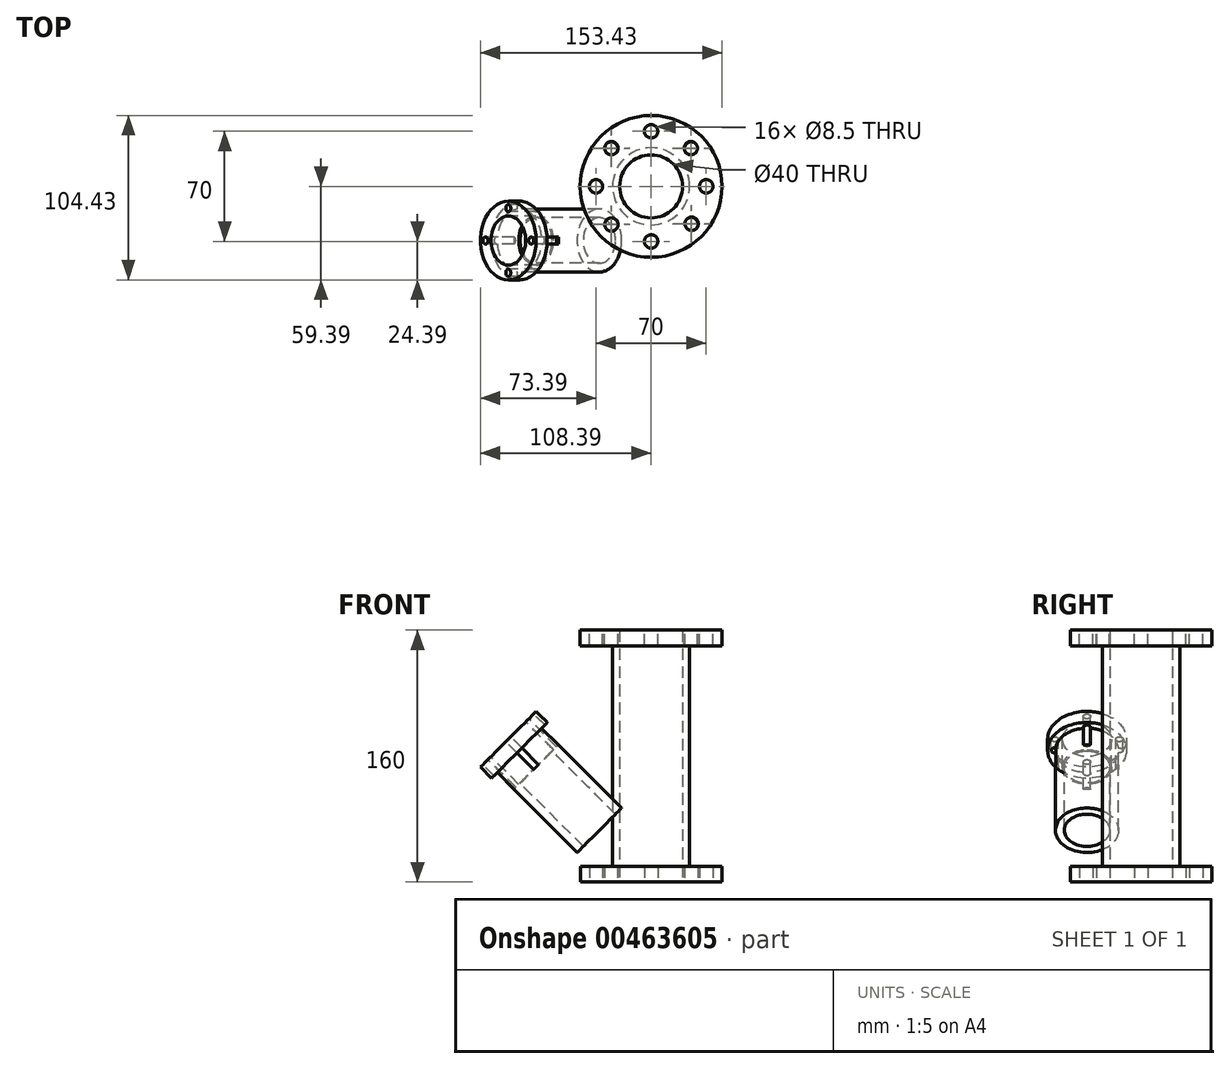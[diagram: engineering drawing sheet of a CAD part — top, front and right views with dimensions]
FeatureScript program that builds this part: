
annotation { "Feature Type Name" : "Feature", "Feature Type Description" : "" }
export const myFeature = defineFeature(function(context is Context, id is Id, definition is map)
    precondition{}
    {
        {
            var Q0;
            Q0=qCreatedBy(makeId("Top.planeOp"),FACE);
            var sketch = newSketch(context, id + "F0", { "sketchPlane" : qUnion([Q0])});
            skCircle(sketch, "E0", {"center": v(0, 0) * mm, "radius": 45 * mm});
            skSolve(sketch);
        }
        {
            var Q0;
            Q0=makeQuery(id+"F0.imprint","IMPRINT",FACE,{"disambiguationData":[TD([[makeQuery(id+"F0.imprint","IMPRINT",EDGE,{"derivedFrom":sQuery(id+"F0.wireOp",EDGE,"E0")}),1.0]])]});
            extrude(context, id + "F1", {"entities" : qUnion([Q0]), "depth" : 10 * mm});
        }
        {
            var Q0;
            Q0=makeQuery(id+"F1.opExtrude","CAP_FACE",FACE,{"disambiguationData":[OSD([sQuery(id+"F0.wireOp",EDGE,"E0")])],"isStart":false});
            var sketch = newSketch(context, id + "F2", { "sketchPlane" : qUnion([Q0])});
            skCircle(sketch, "E1", {"center": v(0, 0) * mm, "radius": 24.5 * mm});
            skSolve(sketch);
        }
        {
            var Q0;
            Q0=makeQuery(id+"F2.imprint","IMPRINT",FACE,{"disambiguationData":[TD([[makeQuery(id+"F2.imprint","IMPRINT",EDGE,{"derivedFrom":sQuery(id+"F2.wireOp",EDGE,"E1")}),1.0]])]});
            extrude(context, id + "F3", {"entities" : qUnion([Q0]), "operationType" : NewBodyOperationType.ADD, "depth" : 140 * mm});
        }
        {
            var Q0;
            Q0=makeQuery(id+"F3.opExtrude","CAP_FACE",FACE,{"disambiguationData":[OSD([sQuery(id+"F2.wireOp",EDGE,"E1")])],"isStart":false});
            var sketch = newSketch(context, id + "F4", { "sketchPlane" : qUnion([Q0])});
            skCircle(sketch, "E2", {"center": v(0, 0) * mm, "radius": 45.04 * mm});
            skSolve(sketch);
        }
        {
            var Q0;
            Q0 = qSketchRegion(id + "F4", true);
            extrude(context, id + "F5", {"entities" : qUnion([Q0]), "operationType" : NewBodyOperationType.ADD, "depth" : 10 * mm});
        }
        {
            var Q0;
            Q0=makeQuery(id+"F1.opExtrude","CAP_FACE",FACE,{"disambiguationData":[OSD([sQuery(id+"F0.wireOp",EDGE,"E0")])],"isStart":true});
            var sketch = newSketch(context, id + "F6", { "sketchPlane" : qUnion([Q0])});
            skCircle(sketch, "E3", {"center": v(0, 0) * mm, "radius": 20 * mm});
            skSolve(sketch);
        }
        {
            var Q0;
            Q0=makeQuery(id+"F6.imprint","IMPRINT",FACE,{"disambiguationData":[TD([[makeQuery(id+"F6.imprint","IMPRINT",EDGE,{"derivedFrom":sQuery(id+"F6.wireOp",EDGE,"E3")}),1.0]])]});
            extrude(context, id + "F7", {"entities" : qUnion([Q0]), "operationType" : NewBodyOperationType.REMOVE, "oppositeDirection" : true, "depth" : 160 * mm});
        }
        {
            var Q0;
            Q0=makeQuery(id+"F5.opExtrude","CAP_FACE",FACE,{"disambiguationData":[OSD([sQuery(id+"F4.wireOp",EDGE,"E2")])],"isStart":false});
            var sketch = newSketch(context, id + "F8", { "sketchPlane" : qUnion([Q0])});
            skCircle(sketch, "E4", {"center": v(0, 35) * mm, "radius": 4.25 * mm});
            skCircle(sketch, "E5", {"center": v(35, 0) * mm, "radius": 4.25 * mm});
            skCircle(sketch, "E6", {"center": v(0, -35) * mm, "radius": 4.25 * mm});
            skCircle(sketch, "E7", {"center": v(-35, 0) * mm, "radius": 4.25 * mm});
            skCircle(sketch, "E8", {"center": v(-25.23, 24.26) * mm, "radius": 4.25 * mm});
            skCircle(sketch, "E9", {"center": v(25.73, -23.73) * mm, "radius": 4.25 * mm});
            skCircle(sketch, "E10", {"center": v(25.23, 24.26) * mm, "radius": 4.25 * mm});
            skCircle(sketch, "E11", {"center": v(-25.23, -24.26) * mm, "radius": 4.25 * mm});
            skSolve(sketch);
        }
        {
            var Q0;
            Q0=makeQuery(id+"F8.imprint","IMPRINT",FACE,{"disambiguationData":[TD([[makeQuery(id+"F8.imprint","IMPRINT",EDGE,{"derivedFrom":sQuery(id+"F8.wireOp",EDGE,"E8")}),1.0]])]});
            var Q1;
            Q1=makeQuery(id+"F8.imprint","IMPRINT",FACE,{"disambiguationData":[TD([[makeQuery(id+"F8.imprint","IMPRINT",EDGE,{"derivedFrom":sQuery(id+"F8.wireOp",EDGE,"E10")}),1.0]])]});
            var Q2;
            Q2=makeQuery(id+"F8.imprint","IMPRINT",FACE,{"disambiguationData":[TD([[makeQuery(id+"F8.imprint","IMPRINT",EDGE,{"derivedFrom":sQuery(id+"F8.wireOp",EDGE,"E4")}),1.0]])]});
            var Q3;
            Q3=makeQuery(id+"F8.imprint","IMPRINT",FACE,{"disambiguationData":[TD([[makeQuery(id+"F8.imprint","IMPRINT",EDGE,{"derivedFrom":sQuery(id+"F8.wireOp",EDGE,"E5")}),1.0]])]});
            var Q4;
            Q4=makeQuery(id+"F8.imprint","IMPRINT",FACE,{"disambiguationData":[TD([[makeQuery(id+"F8.imprint","IMPRINT",EDGE,{"derivedFrom":sQuery(id+"F8.wireOp",EDGE,"E9")}),1.0]])]});
            var Q5;
            Q5=makeQuery(id+"F8.imprint","IMPRINT",FACE,{"disambiguationData":[TD([[makeQuery(id+"F8.imprint","IMPRINT",EDGE,{"derivedFrom":sQuery(id+"F8.wireOp",EDGE,"E6")}),1.0]])]});
            var Q6;
            Q6=makeQuery(id+"F8.imprint","IMPRINT",FACE,{"disambiguationData":[TD([[makeQuery(id+"F8.imprint","IMPRINT",EDGE,{"derivedFrom":sQuery(id+"F8.wireOp",EDGE,"E11")}),1.0]])]});
            var Q7;
            Q7=makeQuery(id+"F8.imprint","IMPRINT",FACE,{"disambiguationData":[TD([[makeQuery(id+"F8.imprint","IMPRINT",EDGE,{"derivedFrom":sQuery(id+"F8.wireOp",EDGE,"E7")}),1.0]])]});
            extrude(context, id + "F9", {"entities" : qUnion([Q0, Q1, Q2, Q3, Q4, Q5, Q6, Q7]), "operationType" : NewBodyOperationType.REMOVE, "oppositeDirection" : true, "depth" : 25 * mm});
        }
        {
            var Q0;
            Q0=makeQuery(id+"F1.opExtrude","CAP_FACE",FACE,{"disambiguationData":[OSD([sQuery(id+"F0.wireOp",EDGE,"E0")])],"isStart":true});
            var sketch = newSketch(context, id + "F10", { "sketchPlane" : qUnion([Q0])});
            skCircle(sketch, "E12", {"center": v(0, 35) * mm, "radius": 4.25 * mm});
            skCircle(sketch, "E13", {"center": v(35, 0) * mm, "radius": 4.25 * mm});
            skCircle(sketch, "E14", {"center": v(0, -35) * mm, "radius": 4.25 * mm});
            skCircle(sketch, "E15", {"center": v(-35, 0) * mm, "radius": 4.25 * mm});
            skCircle(sketch, "E16", {"center": v(-25.46, 24.01) * mm, "radius": 4.25 * mm});
            skCircle(sketch, "E17", {"center": v(25.46, 24.01) * mm, "radius": 4.25 * mm});
            skCircle(sketch, "E18", {"center": v(25.46, -24.01) * mm, "radius": 4.25 * mm});
            skCircle(sketch, "E19", {"center": v(-25.46, -24.01) * mm, "radius": 4.25 * mm});
            skPoint(sketch, "E20.center.orphan", {"position": v(0, 0) * mm});
            skSolve(sketch);
        }
        {
            var Q0;
            Q0=makeQuery(id+"F10.imprint","IMPRINT",FACE,{"disambiguationData":[TD([[makeQuery(id+"F10.imprint","IMPRINT",EDGE,{"derivedFrom":sQuery(id+"F10.wireOp",EDGE,"E16")}),1.0]])]});
            var Q1;
            Q1=makeQuery(id+"F10.imprint","IMPRINT",FACE,{"disambiguationData":[TD([[makeQuery(id+"F10.imprint","IMPRINT",EDGE,{"derivedFrom":sQuery(id+"F10.wireOp",EDGE,"E12")}),1.0]])]});
            var Q2;
            Q2=makeQuery(id+"F10.imprint","IMPRINT",FACE,{"disambiguationData":[TD([[makeQuery(id+"F10.imprint","IMPRINT",EDGE,{"derivedFrom":sQuery(id+"F10.wireOp",EDGE,"E17")}),1.0]])]});
            var Q3;
            Q3=makeQuery(id+"F10.imprint","IMPRINT",FACE,{"disambiguationData":[TD([[makeQuery(id+"F10.imprint","IMPRINT",EDGE,{"derivedFrom":sQuery(id+"F10.wireOp",EDGE,"E13")}),1.0]])]});
            var Q4;
            Q4=makeQuery(id+"F10.imprint","IMPRINT",FACE,{"disambiguationData":[TD([[makeQuery(id+"F10.imprint","IMPRINT",EDGE,{"derivedFrom":sQuery(id+"F10.wireOp",EDGE,"E18")}),1.0]])]});
            var Q5;
            Q5=makeQuery(id+"F10.imprint","IMPRINT",FACE,{"disambiguationData":[TD([[makeQuery(id+"F10.imprint","IMPRINT",EDGE,{"derivedFrom":sQuery(id+"F10.wireOp",EDGE,"E14")}),1.0]])]});
            var Q6;
            Q6=makeQuery(id+"F10.imprint","IMPRINT",FACE,{"disambiguationData":[TD([[makeQuery(id+"F10.imprint","IMPRINT",EDGE,{"derivedFrom":sQuery(id+"F10.wireOp",EDGE,"E19")}),1.0]])]});
            var Q7;
            Q7=makeQuery(id+"F10.imprint","IMPRINT",FACE,{"disambiguationData":[TD([[makeQuery(id+"F10.imprint","IMPRINT",EDGE,{"derivedFrom":sQuery(id+"F10.wireOp",EDGE,"E15")}),1.0]])]});
            extrude(context, id + "F11", {"entities" : qUnion([Q0, Q1, Q2, Q3, Q4, Q5, Q6, Q7]), "operationType" : NewBodyOperationType.REMOVE, "oppositeDirection" : true, "depth" : 25 * mm});
        }
        {
            var Q0;
            Q0=qCreatedBy(makeId("Front.planeOp"),FACE);
            var sketch = newSketch(context, id + "F12", { "sketchPlane" : qUnion([Q0])});
            skLineSegment(sketch, "E21", {"start": v(0, 0) * mm, "end": v(0, 40) * mm});
            skLineSegment(sketch, "E22", {"start": v(0, 40) * mm, "end": v(-63.64, 103.64) * mm});
            skLineSegment(sketch, "E23", {"start": v(-63.64, 103.64) * mm, "end": v(-53.98, 113.3) * mm});
            skSolve(sketch);
        }
        {
            var Q0;
            Q0=qCreatedBy(makeId("Right.planeOp"),FACE);
            var Q1;
            Q1=sQuery(id+"F12.wireOp",EDGE,"E23");
            cPlane(context, id + "F13", {"entities" : qUnion([Q0, Q1]), "cplaneType" : CPlaneType.LINE_ANGLE, "offset" : 25 * mm, "angle" : 0 * degree, "width" : 150 * mm, "height" : 150 * mm});
        }
        {
            var Q0;
            Q0=qCreatedBy(id+"F13.planeOp",FACE);
            var sketch = newSketch(context, id + "F14", { "sketchPlane" : qUnion([Q0])});
            skCircle(sketch, "E24", {"center": v(34.4, 0) * mm, "radius": 20 * mm});
            skSolve(sketch);
        }
        {
            var Q0;
            Q0 = qSketchRegion(id + "F14", true);
            extrude(context, id + "F15", {"entities" : qUnion([Q0]), "operationType" : NewBodyOperationType.ADD, "oppositeDirection" : true, "depth" : 71.8 * mm});
        }
        {
            var Q0;
            Q0=makeQuery(id+"F15.opExtrude","CAP_FACE",FACE,{"disambiguationData":[OSD([sQuery(id+"F14.wireOp",EDGE,"E24")])],"isStart":true});
            var sketch = newSketch(context, id + "F16", { "sketchPlane" : qUnion([Q0])});
            skCircle(sketch, "E25", {"center": v(34.4, 0) * mm, "radius": 25 * mm});
            skSolve(sketch);
        }
        {
            var Q0;
            Q0 = qSketchRegion(id + "F16", true);
            extrude(context, id + "F17", {"entities" : qUnion([Q0]), "operationType" : NewBodyOperationType.ADD, "depth" : 10 * mm});
        }
        {
            var Q0;
            Q0=makeQuery(id+"F17.opExtrude","CAP_FACE",FACE,{"disambiguationData":[OSD([sQuery(id+"F16.wireOp",EDGE,"E25")])],"isStart":false});
            var sketch = newSketch(context, id + "F18", { "sketchPlane" : qUnion([Q0])});
            skCircle(sketch, "E26", {"center": v(34.4, 0) * mm, "radius": 14.46 * mm});
            skSolve(sketch);
        }
        {
            var Q0;
            Q0=makeQuery(id+"F18.imprint","IMPRINT",FACE,{"disambiguationData":[TD([[makeQuery(id+"F18.imprint","IMPRINT",EDGE,{"derivedFrom":sQuery(id+"F18.wireOp",EDGE,"E26")}),1.0]])]});
            var Q1;
            Q1=sQuery(id+"F18.wireOp",EDGE,"E26");
            extrude(context, id + "F19", {"entities" : qUnion([Q0]), "operationType" : NewBodyOperationType.REMOVE, "surfaceEntities" : qUnion([Q1]), "oppositeDirection" : true, "depth" : 98.5 * mm});
        }
        {
            var Q0;
            Q0=makeQuery(id+"F17.opExtrude","CAP_FACE",FACE,{"disambiguationData":[OSD([sQuery(id+"F16.wireOp",EDGE,"E25")])],"isStart":false});
            var sketch = newSketch(context, id + "F20", { "sketchPlane" : qUnion([Q0])});
            skCircle(sketch, "E27", {"center": v(34.4, 0) * mm, "radius": 15.6 * mm});
            skSolve(sketch);
        }
        {
            var Q0;
            Q0=makeQuery(id+"F20.imprint","IMPRINT",FACE,{"disambiguationData":[TD([[makeQuery(id+"F20.imprint","IMPRINT",EDGE,{"derivedFrom":sQuery(id+"F20.wireOp",EDGE,"E27")}),1.0]])]});
            extrude(context, id + "F21", {"entities" : qUnion([Q0]), "operationType" : NewBodyOperationType.REMOVE, "oppositeDirection" : true, "depth" : 25 * mm});
        }
        {
            var Q0;
            Q0=makeQuery(id+"F17.opExtrude","CAP_FACE",FACE,{"disambiguationData":[OSD([sQuery(id+"F16.wireOp",EDGE,"E25")])],"isStart":false});
            var sketch = newSketch(context, id + "F22", { "sketchPlane" : qUnion([Q0])});
            skCircle(sketch, "E28", {"center": v(54.9, 0) * mm, "radius": 2.25 * mm});
            skCircle(sketch, "E29", {"center": v(13.87, 0) * mm, "radius": 2.25 * mm});
            skCircle(sketch, "E30", {"center": v(34.4, -20.52) * mm, "radius": 2.25 * mm});
            skCircle(sketch, "E31", {"center": v(34.4, 20.52) * mm, "radius": 2.25 * mm});
            skPoint(sketch, "E32.center.orphan", {"position": v(34.4, 0) * mm});
            skSolve(sketch);
        }
        {
            var Q0;
            Q0=makeQuery(id+"F22.imprint","IMPRINT",FACE,{"disambiguationData":[TD([[makeQuery(id+"F22.imprint","IMPRINT",EDGE,{"derivedFrom":sQuery(id+"F22.wireOp",EDGE,"E28")}),1.0]])]});
            var Q1;
            Q1=makeQuery(id+"F22.imprint","IMPRINT",FACE,{"disambiguationData":[TD([[makeQuery(id+"F22.imprint","IMPRINT",EDGE,{"derivedFrom":sQuery(id+"F22.wireOp",EDGE,"E30")}),1.0]])]});
            var Q2;
            Q2=makeQuery(id+"F22.imprint","IMPRINT",FACE,{"disambiguationData":[TD([[makeQuery(id+"F22.imprint","IMPRINT",EDGE,{"derivedFrom":sQuery(id+"F22.wireOp",EDGE,"E29")}),1.0]])]});
            var Q3;
            Q3=makeQuery(id+"F22.imprint","IMPRINT",FACE,{"disambiguationData":[TD([[makeQuery(id+"F22.imprint","IMPRINT",EDGE,{"derivedFrom":sQuery(id+"F22.wireOp",EDGE,"E31")}),1.0]])]});
            extrude(context, id + "F23", {"entities" : qUnion([Q0, Q1, Q2, Q3]), "operationType" : NewBodyOperationType.REMOVE, "oppositeDirection" : true, "depth" : 25 * mm});
        }
    });
